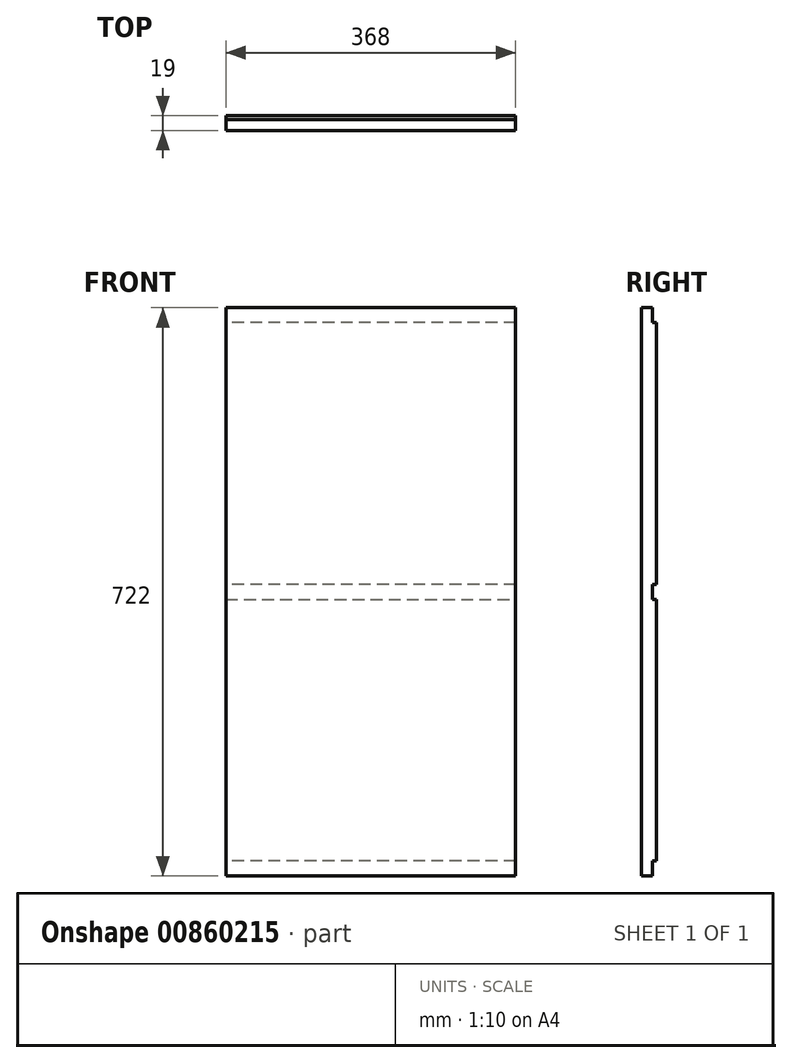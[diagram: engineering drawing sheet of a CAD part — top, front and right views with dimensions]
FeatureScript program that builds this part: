
annotation { "Feature Type Name" : "Feature", "Feature Type Description" : "" }
export const myFeature = defineFeature(function(context is Context, id is Id, definition is map)
    precondition{}
    {
        {
            var Q0;
            Q0=qCreatedBy(makeId("Front.planeOp"),FACE);
            var sketch = newSketch(context, id + "F0", { "sketchPlane" : qUnion([Q0])});
            skLineSegment(sketch, "E0.bottom", {"start": v(0, 0) * mm, "end": v(368, 0) * mm});
            skLineSegment(sketch, "E0.top", {"start": v(0, 722) * mm, "end": v(368, 722) * mm});
            skLineSegment(sketch, "E0.left", {"start": v(0, 0) * mm, "end": v(0, 722) * mm});
            skLineSegment(sketch, "E0.right", {"start": v(368, 0) * mm, "end": v(368, 722) * mm});
            skSolve(sketch);
        }
        {
            var Q0;
            Q0=makeQuery(id+"F0.imprint","IMPRINT",FACE,{"disambiguationData":[TD([[makeQuery(id+"F0.imprint","IMPRINT",EDGE,{"derivedFrom":sQuery(id+"F0.wireOp",EDGE,"E0.bottom")}),1.0]])]});
            extrude(context, id + "F1", {"entities" : qUnion([Q0]), "depth" : 19 * mm, "offsetDistance" : 25 * mm});
        }
        {
            var Q0;
            Q0=makeQuery(id+"F1.opExtrude","CAP_FACE",FACE,{"disambiguationData":[OSD([sQuery(id+"F0.wireOp",EDGE,"E0.bottom"),sQuery(id+"F0.wireOp",EDGE,"E0.top"),sQuery(id+"F0.wireOp",EDGE,"E0.left"),sQuery(id+"F0.wireOp",EDGE,"E0.right")])],"isStart":true});
            var sketch = newSketch(context, id + "F2", { "sketchPlane" : qUnion([Q0])});
            skLineSegment(sketch, "E1", {"start": v(-368, 361) * mm, "end": v(-368, 370.5) * mm});
            skLineSegment(sketch, "E2", {"start": v(-368, 370.5) * mm, "end": v(0, 370.5) * mm});
            skLineSegment(sketch, "E3", {"start": v(0, 370.5) * mm, "end": v(0, 361) * mm});
            skLineSegment(sketch, "E4", {"start": v(0, 361) * mm, "end": v(0, 351.5) * mm});
            skLineSegment(sketch, "E5", {"start": v(0, 351.5) * mm, "end": v(-368, 351.5) * mm});
            skLineSegment(sketch, "E6", {"start": v(-368, 351.5) * mm, "end": v(-368, 361) * mm});
            skLineSegment(sketch, "E7.bottom", {"start": v(-368, 0) * mm, "end": v(0, 0) * mm});
            skLineSegment(sketch, "E7.top", {"start": v(-368, 19) * mm, "end": v(0, 19) * mm});
            skLineSegment(sketch, "E7.left", {"start": v(-368, 0) * mm, "end": v(-368, 19) * mm});
            skLineSegment(sketch, "E7.right", {"start": v(0, 0) * mm, "end": v(0, 19) * mm});
            skLineSegment(sketch, "E8.bottom", {"start": v(-368, 722) * mm, "end": v(0, 722) * mm});
            skLineSegment(sketch, "E8.top", {"start": v(-368, 703) * mm, "end": v(0, 703) * mm});
            skLineSegment(sketch, "E8.left", {"start": v(-368, 722) * mm, "end": v(-368, 703) * mm});
            skLineSegment(sketch, "E8.right", {"start": v(0, 722) * mm, "end": v(0, 703) * mm});
            skSolve(sketch);
        }
        {
            var Q0;
            Q0 = qSketchRegion(id + "F2", true);
            extrude(context, id + "F3", {"entities" : qUnion([Q0]), "operationType" : NewBodyOperationType.REMOVE, "oppositeDirection" : true, "depth" : 5 * mm, "offsetDistance" : 25 * mm});
        }
    });
